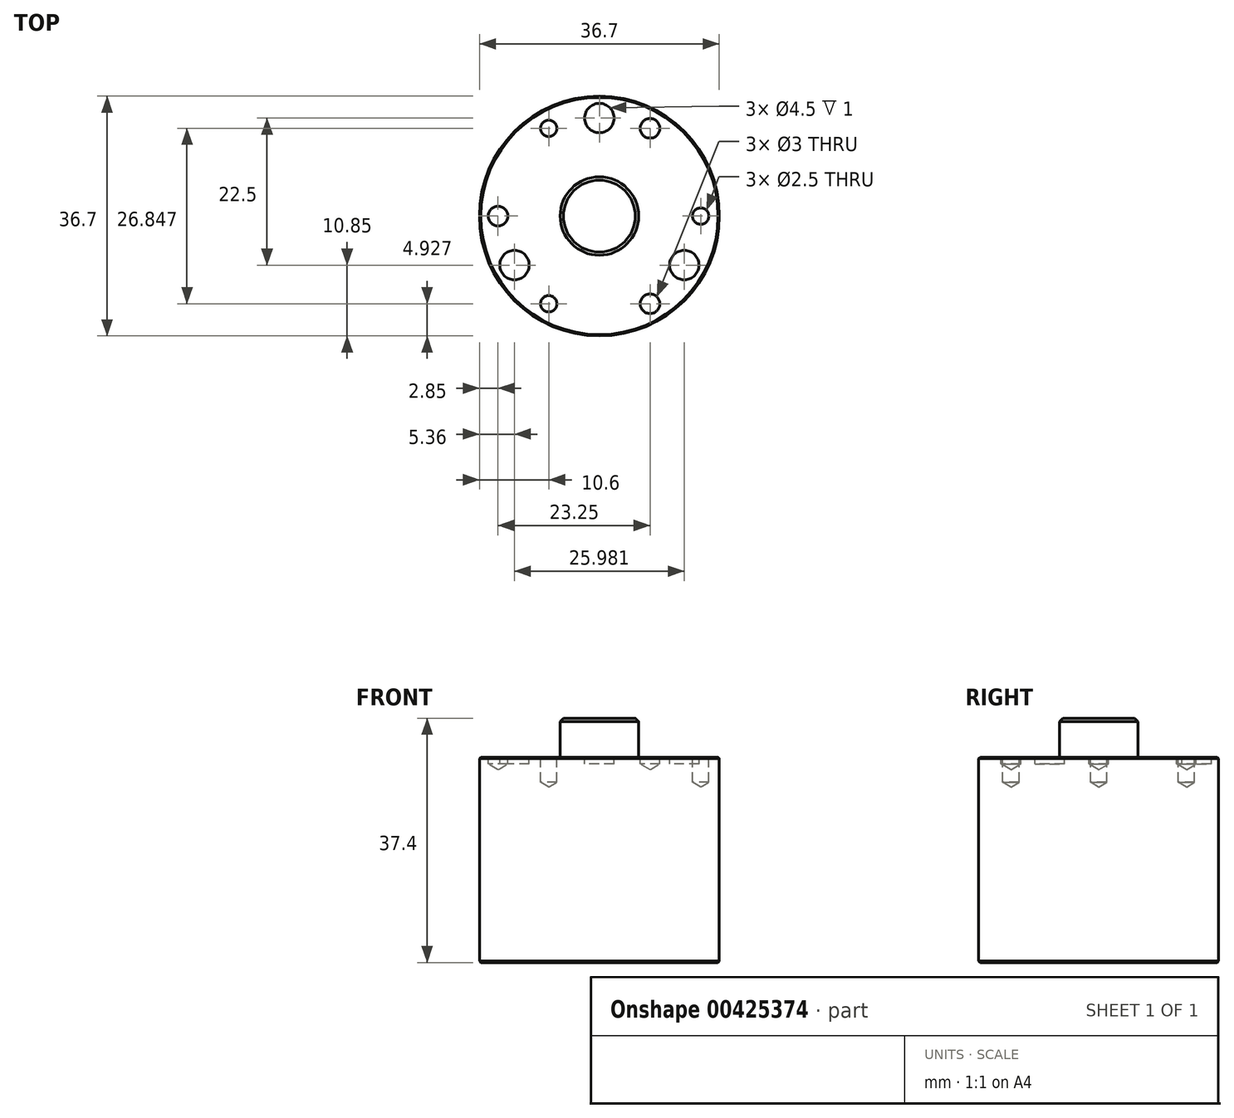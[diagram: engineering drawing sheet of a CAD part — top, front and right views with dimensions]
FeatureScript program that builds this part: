
annotation { "Feature Type Name" : "Feature", "Feature Type Description" : "" }
export const myFeature = defineFeature(function(context is Context, id is Id, definition is map)
    precondition{}
    {
        {
            var Q0;
            Q0=qCreatedBy(makeId("Top.planeOp"),FACE);
            var sketch = newSketch(context, id + "F0", { "sketchPlane" : qUnion([Q0])});
            skCircle(sketch, "E0", {"center": v(0, 0) * mm, "radius": 18.35 * mm});
            skSolve(sketch);
        }
        {
            var Q0;
            Q0 = qSketchRegion(id + "F0", true);
            extrude(context, id + "F1", {"entities" : qUnion([Q0]), "oppositeDirection" : true, "depth" : 31.4 * mm, "offsetDistance" : 25 * mm});
        }
        {
            var Q0;
            Q0=qCreatedBy(makeId("Top.planeOp"),FACE);
            var sketch = newSketch(context, id + "F2", { "sketchPlane" : qUnion([Q0])});
            skCircle(sketch, "E1", {"center": v(0, 0) * mm, "radius": 6 * mm});
            skSolve(sketch);
        }
        {
            var Q0;
            Q0=makeQuery(id+"F2.imprint","IMPRINT",FACE,{"disambiguationData":[TD([[makeQuery(id+"F2.imprint","IMPRINT",EDGE,{"derivedFrom":sQuery(id+"F2.wireOp",EDGE,"E1")}),1.0]])]});
            extrude(context, id + "F3", {"entities" : qUnion([Q0]), "operationType" : NewBodyOperationType.ADD, "depth" : 6 * mm});
        }
        {
            var Q0;
            Q0=makeQuery(id+"F3.opExtrude","CAP_EDGE",EDGE,{"disambiguationData":[OSD([sQuery(id+"F2.wireOp",EDGE,"E1")])],"isStart":false});
            chamfer(context, id + "F4", {"entities" : qUnion([Q0]), "width" : 0.5 * mm, "tangentPropagation" : true});
        }
        {
            var Q0;
            Q0=makeQuery(id+"F1.opExtrude","CAP_EDGE",EDGE,{"disambiguationData":[OSD([sQuery(id+"F0.wireOp",EDGE,"E0")])],"isStart":true});
            var Q1;
            Q1=makeQuery(id+"F1.opExtrude","CAP_EDGE",EDGE,{"disambiguationData":[OSD([sQuery(id+"F0.wireOp",EDGE,"E0")])],"isStart":false});
            chamfer(context, id + "F5", {"entities" : qUnion([Q0, Q1]), "width" : 0.2 * mm, "tangentPropagation" : true});
        }
        {
            var Q0;
            Q0=qCreatedBy(makeId("Top.planeOp"),FACE);
            var sketch = newSketch(context, id + "F6", { "sketchPlane" : qUnion([Q0])});
            skCircle(sketch, "E2", {"center": v(0, 0) * mm, "radius": 15 * mm, "construction": true});
            skCircle(sketch, "E3", {"center": v(0, 15) * mm, "radius": 2.25 * mm});
            skCircle(sketch, "E4.1.0", {"center": v(-13, -7.5) * mm, "radius": 2.25 * mm});
            skCircle(sketch, "E4.2.0", {"center": v(13, -7.5) * mm, "radius": 2.25 * mm});
            skLineSegment(sketch, "E5", {"start": v(0, 0) * mm, "end": v(0, 15) * mm, "construction": true});
            skSolve(sketch);
        }
        {
            var Q0;
            Q0 = qSketchRegion(id + "F6", true);
            extrude(context, id + "F7", {"entities" : qUnion([Q0]), "operationType" : NewBodyOperationType.REMOVE, "oppositeDirection" : true, "depth" : 1 * mm});
        }
        {
            var Q0;
            Q0=qCreatedBy(makeId("Top.planeOp"),FACE);
            var sketch = newSketch(context, id + "F8", { "sketchPlane" : qUnion([Q0])});
            skCircle(sketch, "E6", {"center": v(0, 0) * mm, "radius": 15.5 * mm, "construction": true});
            skPoint(sketch, "E7", {"position": v(7.75, 13.42) * mm});
            skLineSegment(sketch, "E8", {"start": v(0, 15.5) * mm, "end": v(0, 0) * mm, "construction": true});
            skLineSegment(sketch, "E9", {"start": v(0, 0) * mm, "end": v(7.75, 13.42) * mm, "construction": true});
            skPoint(sketch, "E10.1.0", {"position": v(-15.5, 0) * mm});
            skPoint(sketch, "E10.2.0", {"position": v(7.75, -13.42) * mm});
            skSolve(sketch);
        }
        {
            var Q0;
            Q0=sQuery(id+"F8.wireOp",VERTEX,"E7");
            var Q1;
            Q1=sQuery(id+"F8.wireOp",VERTEX,"E10.2.0");
            var Q2;
            Q2=sQuery(id+"F8.wireOp",VERTEX,"E10.1.0");
            var Q3;
            Q3=makeQuery(id+"F1.opExtrude","SWEPT_BODY",BODY,{"disambiguationData":[OSD([sQuery(id+"F0.wireOp",EDGE,"E0")])]});
            hole(context, id + "F9", {"style" : HoleStyle.SIMPLE, "endStyle" : HoleEndStyle.BLIND, "standardTappedOrClearance" : lookupTablePath({ "standard" : "ISO", "size" : "3", "type" : "Drilled" }), "standardBlindInLast" : lookupTablePath({ "standard" : "ISO", "size" : "3", "type" : "Drilled" }), "holeDiameter" : 3 * mm, "holeDepth" : 1 * mm, "isTappedThrough" : true, "tappedDepth" : 12 * mm, "tapClearance" : 3, "startFromSketch" : true, "locations" : qUnion([Q0, Q1, Q2]), "scope" : qUnion([Q3])});
        }
        {
            var Q0;
            Q0=qCreatedBy(makeId("Top.planeOp"),FACE);
            var sketch = newSketch(context, id + "F10", { "sketchPlane" : qUnion([Q0])});
            skCircle(sketch, "E11", {"center": v(0, 0) * mm, "radius": 15.5 * mm, "construction": true});
            skPoint(sketch, "E12", {"position": v(-7.75, 13.42) * mm});
            skLineSegment(sketch, "E13", {"start": v(-7.75, 13.42) * mm, "end": v(0, 0) * mm, "construction": true});
            skLineSegment(sketch, "E14", {"start": v(0, 0) * mm, "end": v(0, 15.5) * mm, "construction": true});
            skPoint(sketch, "E15.1.0", {"position": v(-7.75, -13.42) * mm});
            skPoint(sketch, "E15.2.0", {"position": v(15.5, 0) * mm});
            skSolve(sketch);
        }
        {
            var Q0;
            Q0=sQuery(id+"F10.wireOp",VERTEX,"E12");
            var Q1;
            Q1=sQuery(id+"F10.wireOp",VERTEX,"E15.2.0");
            var Q2;
            Q2=sQuery(id+"F10.wireOp",VERTEX,"E15.1.0");
            var Q3;
            Q3=makeQuery(id+"F1.opExtrude","SWEPT_BODY",BODY,{"disambiguationData":[OSD([sQuery(id+"F0.wireOp",EDGE,"E0")])]});
            hole(context, id + "F11", {"style" : HoleStyle.SIMPLE, "endStyle" : HoleEndStyle.BLIND, "standardTappedOrClearance" : lookupTablePath({ "standard" : "ISO", "engagement" : "75%", "pitch" : "0.5 mm", "size" : "M3", "type" : "Tapped" }), "standardBlindInLast" : lookupTablePath({ "standard" : "ISO", "engagement" : "75%", "pitch" : "0.5 mm", "size" : "M3", "type" : "Tapped" }), "holeDiameter" : 2.5 * mm, "showTappedDepth" : true, "holeDepth" : 3.8 * mm, "isTappedThrough" : true, "tappedDepth" : 2.3 * mm, "tapClearance" : 3, "startFromSketch" : true, "locations" : qUnion([Q0, Q1, Q2]), "scope" : qUnion([Q3]), "majorDiameter" : 3 * mm});
        }
    });
